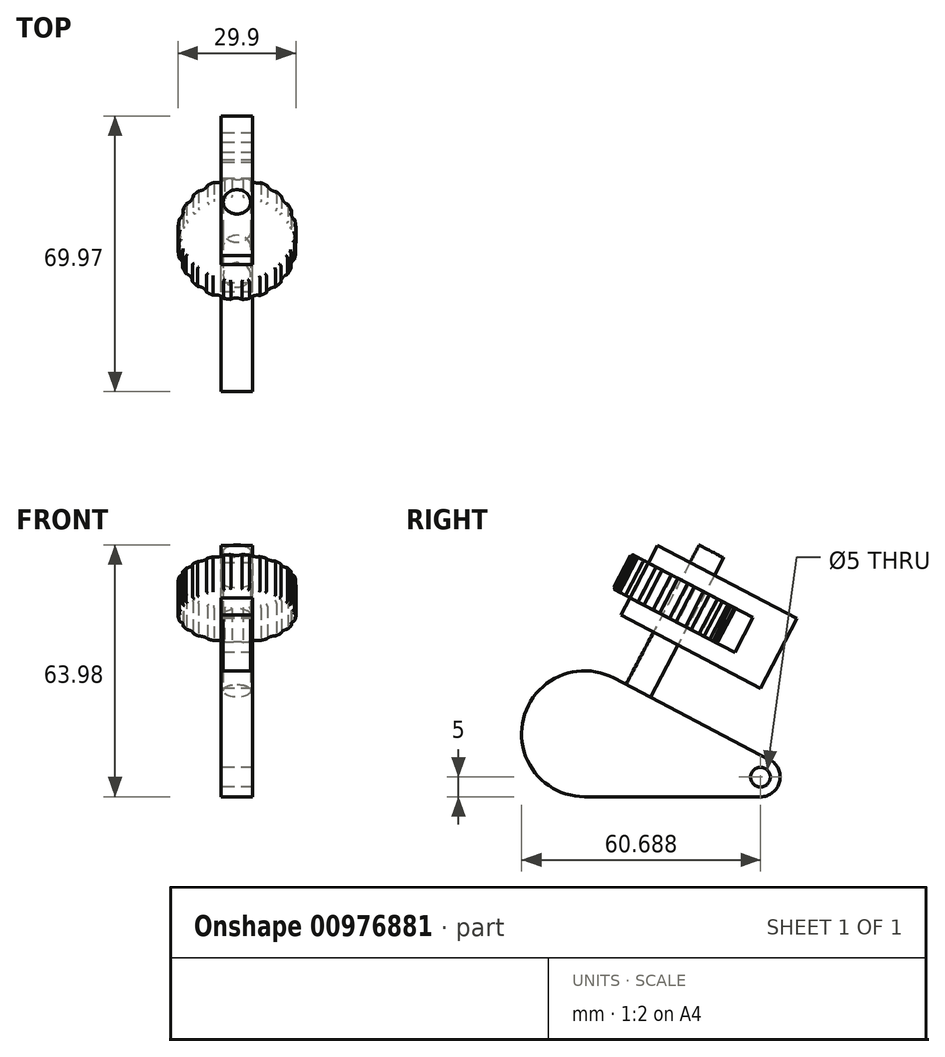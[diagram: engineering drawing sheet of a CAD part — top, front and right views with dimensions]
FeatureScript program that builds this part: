
annotation { "Feature Type Name" : "Feature", "Feature Type Description" : "" }
export const myFeature = defineFeature(function(context is Context, id is Id, definition is map)
    precondition{}
    {
        {
            var Q0;
            Q0=qCreatedBy(makeId("Right.planeOp"),FACE);
            var sketch = newSketch(context, id + "F0", { "sketchPlane" : qUnion([Q0])});
            skCircle(sketch, "E0", {"center": v(0, 0) * mm, "radius": 16 * mm});
            skLineSegment(sketch, "E1", {"start": v(35.46, -16) * mm, "end": v(40.22, -16) * mm});
            skLineSegment(sketch, "E2", {"start": v(47, -6.57) * mm, "end": v(7.43, 14.17) * mm});
            skPoint(sketch, "E3.visualSharp", {"position": v(65, -16) * mm});
            skArc(sketch, "E3.filletArc", {"start": v(44.69, -16) * mm, "mid": v(49.54, -12.2) * mm, "end": v(47, -6.57) * mm});
            skCircle(sketch, "E4", {"center": v(44.69, -11) * mm, "radius": 2.5 * mm});
            skCircle(sketch, "E5", {"center": v(0, 0) * mm, "radius": 35 * mm, "construction": true});
            skArc(sketch, "E6", {"start": v(34.54, -14.61) * mm, "mid": v(35.92, -10.78) * mm, "end": v(36.87, -6.82) * mm});
            skArc(sketch, "E7", {"start": v(40.96, -7.67) * mm, "mid": v(39.69, -11) * mm, "end": v(40.96, -14.33) * mm});
            skLineSegment(sketch, "E8", {"start": v(40.22, -6) * mm, "end": v(37.86, -6) * mm});
            skPoint(sketch, "E9.visualSharp", {"position": v(44.69, -6) * mm});
            skArc(sketch, "E9.filletArc", {"start": v(40.96, -7.67) * mm, "mid": v(41.13, -6.6) * mm, "end": v(40.22, -6) * mm});
            skPoint(sketch, "E10.visualSharp", {"position": v(37.02, -6) * mm});
            skArc(sketch, "E10.filletArc", {"start": v(37.86, -6) * mm, "mid": v(37.22, -6.23) * mm, "end": v(36.87, -6.82) * mm});
            skPoint(sketch, "E11.visualSharp", {"position": v(44.69, -16) * mm});
            skArc(sketch, "E11.filletArc", {"start": v(40.22, -16) * mm, "mid": v(41.13, -15.4) * mm, "end": v(40.96, -14.33) * mm});
            skPoint(sketch, "E12.newPointB", {"position": v(0, -16) * mm});
            skArc(sketch, "E12.filletArc", {"start": v(34.54, -14.61) * mm, "mid": v(34.62, -15.55) * mm, "end": v(35.46, -16) * mm});
            skLineSegment(sketch, "E13", {"start": v(35.46, -16) * mm, "end": v(0, -16) * mm});
            skLineSegment(sketch, "E14", {"start": v(40.22, -16) * mm, "end": v(44.69, -16) * mm});
            skSolve(sketch);
        }
        {
            var Q0;
            {var subQ0=sQuery(id+"F0.wireOp",EDGE,"E0");var subQ1=makeQuery(id+"F0.imprint","INTERSECT",VERTEX,{"derivedFrom":[subQ0,sQuery(id+"F0.wireOp",EDGE,"E2")]});Q0=makeQuery(id+"F0.imprint","IMPRINT",FACE,{"disambiguationData":[TD([[makeQuery(id+"F0.imprint","IMPRINT",EDGE,{"disambiguationData":[TD([[subQ1,-1.0]])],"derivedFrom":subQ0}),1.0]])]});}
            var Q1;
            {var subQ0=sQuery(id+"F0.wireOp",EDGE,"E2");Q1=makeQuery(id+"F0.imprint","IMPRINT",FACE,{"disambiguationData":[TD([[makeQuery(id+"F0.imprint","IMPRINT",EDGE,{"derivedFrom":subQ0}),1.0]])]});}
            var Q2;
            Q2=makeQuery(id+"F0.imprint","IMPRINT",FACE,{"disambiguationData":[TD([[makeQuery(id+"F0.imprint","IMPRINT",EDGE,{"derivedFrom":sQuery(id+"F0.wireOp",EDGE,"E1")}),1.0]])]});
            extrude(context, id + "F1", {"entities" : qUnion([Q0, Q1, Q2]), "depth" : 8 * mm, "offsetDistance" : 25 * mm});
        }
        {
            var Q0;
            Q0=makeQuery(id+"F1.opExtrude","SWEPT_FACE",FACE,{"disambiguationData":[OSD([sQuery(id+"F0.wireOp",EDGE,"E2")])]});
            var sketch = newSketch(context, id + "F2", { "sketchPlane" : qUnion([Q0])});
            skCircle(sketch, "E15", {"center": v(4, 7) * mm, "radius": 3.5 * mm});
            skPoint(sketch, "E15.centerSnap0", {"position": v(4, 0) * mm});
            skSolve(sketch);
        }
        {
            var Q0;
            {var subQ0=sQuery(id+"F2.wireOp",EDGE,"E15");var subQ1=sQuery(id+"F0.wireOp",EDGE,"E2");var subQ2=makeQuery(id+"F2.imprint","INTERSECT",VERTEX,{"derivedFrom":[makeQuery(id+"F1.opExtrude","CAP_EDGE",EDGE,{"disambiguationData":[OSD([subQ1])],"isStart":true}),subQ0]});Q0=makeQuery(id+"F2.imprint","IMPRINT",FACE,{"disambiguationData":[TD([[makeQuery(id+"F2.imprint","IMPRINT",EDGE,{"disambiguationData":[TD([[subQ2,1.0]])],"derivedFrom":subQ0}),1.0]])]});}
            extrude(context, id + "F3", {"entities" : qUnion([Q0]), "depth" : 40 * mm, "offsetDistance" : 25 * mm});
        }
        {
            var Q0;
            Q0=qCreatedBy(makeId("Right.planeOp"),FACE);
            var sketch = newSketch(context, id + "F4", { "sketchPlane" : qUnion([Q0])});
            skLineSegment(sketch, "E16", {"start": v(9.26, 30.15) * mm, "end": v(44.69, 11.58) * mm});
            skLineSegment(sketch, "E17", {"start": v(9.26, 30.15) * mm, "end": v(11.58, 34.58) * mm});
            skLineSegment(sketch, "E18", {"start": v(11.58, 34.58) * mm, "end": v(38.15, 20.65) * mm});
            skLineSegment(sketch, "E19", {"start": v(38.15, 20.65) * mm, "end": v(42.8, 29.5) * mm});
            skLineSegment(sketch, "E20", {"start": v(42.8, 29.5) * mm, "end": v(16.22, 43.43) * mm});
            skLineSegment(sketch, "E21", {"start": v(16.22, 43.43) * mm, "end": v(18.54, 47.86) * mm});
            skLineSegment(sketch, "E22", {"start": v(18.54, 47.86) * mm, "end": v(53.97, 29.3) * mm});
            skLineSegment(sketch, "E23", {"start": v(53.97, 29.3) * mm, "end": v(44.69, 11.58) * mm});
            skSolve(sketch);
        }
        {
            var Q0;
            Q0=makeQuery(id+"F4.imprint","IMPRINT",FACE,{"disambiguationData":[TD([[makeQuery(id+"F4.imprint","IMPRINT",EDGE,{"derivedFrom":sQuery(id+"F4.wireOp",EDGE,"E16")}),1.0]])]});
            extrude(context, id + "F5", {"entities" : qUnion([Q0]), "depth" : 8 * mm, "offsetDistance" : 25 * mm});
        }
        {
            var Q0;
            Q0=makeQuery(id+"F5.opExtrude","SWEPT_FACE",FACE,{"disambiguationData":[OSD([sQuery(id+"F4.wireOp",EDGE,"E18")])]});
            var sketch = newSketch(context, id + "F6", { "sketchPlane" : qUnion([Q0])});
            skCircle(sketch, "E24", {"center": v(4, 4.2) * mm, "radius": 15 * mm});
            skPoint(sketch, "E24.centerSnap0", {"position": v(4, -5.8) * mm});
            skLineSegment(sketch, "E25", {"start": v(3.83, -10.8) * mm, "end": v(3.83, -12.8) * mm});
            skCircle(sketch, "E26", {"center": v(3.83, -12.8) * mm, "radius": 2.5 * mm});
            skCircle(sketch, "E27.1.0", {"center": v(9.1, -12.01) * mm, "radius": 2.5 * mm});
            skCircle(sketch, "E27.2.0", {"center": v(13.86, -9.64) * mm, "radius": 2.5 * mm});
            skCircle(sketch, "E27.3.0", {"center": v(17.66, -5.92) * mm, "radius": 2.5 * mm});
            skCircle(sketch, "E27.4.0", {"center": v(20.12, -1.2) * mm, "radius": 2.5 * mm});
            skCircle(sketch, "E27.5.0", {"center": v(21, 4.04) * mm, "radius": 2.5 * mm});
            skCircle(sketch, "E27.6.0", {"center": v(20.22, 9.3) * mm, "radius": 2.5 * mm});
            skCircle(sketch, "E27.7.0", {"center": v(17.85, 14.06) * mm, "radius": 2.5 * mm});
            skCircle(sketch, "E27.8.0", {"center": v(14.13, 17.86) * mm, "radius": 2.5 * mm});
            skCircle(sketch, "E27.9.0", {"center": v(9.41, 20.32) * mm, "radius": 2.5 * mm});
            skCircle(sketch, "E27.10.0", {"center": v(4.17, 21.2) * mm, "radius": 2.5 * mm});
            skCircle(sketch, "E27.11.0", {"center": v(-1.1, 20.42) * mm, "radius": 2.5 * mm});
            skCircle(sketch, "E27.12.0", {"center": v(-5.86, 18.06) * mm, "radius": 2.5 * mm});
            skCircle(sketch, "E27.13.0", {"center": v(-9.66, 14.33) * mm, "radius": 2.5 * mm});
            skCircle(sketch, "E27.14.0", {"center": v(-12.12, 9.62) * mm, "radius": 2.5 * mm});
            skCircle(sketch, "E27.15.0", {"center": v(-13, 4.37) * mm, "radius": 2.5 * mm});
            skCircle(sketch, "E27.16.0", {"center": v(-12.22, -0.89) * mm, "radius": 2.5 * mm});
            skCircle(sketch, "E27.17.0", {"center": v(-9.85, -5.65) * mm, "radius": 2.5 * mm});
            skCircle(sketch, "E27.18.0", {"center": v(-6.13, -9.45) * mm, "radius": 2.5 * mm});
            skCircle(sketch, "E27.19.0", {"center": v(-1.41, -11.9) * mm, "radius": 2.5 * mm});
            skCircle(sketch, "E28", {"center": v(4, 4.2) * mm, "radius": 3.5 * mm});
            skSolve(sketch);
        }
        {
            var Q0;
            {var subQ56=sQuery(id+"F4.wireOp",EDGE,"E18");var subQ57=makeQuery(id+"F5.opExtrude","SWEPT_EDGE",EDGE,{"disambiguationData":[OSD([sQuery(id+"F4.wireOp",EDGE,"E17"),subQ56])]});Q0=makeQuery(id+"F6.imprint","IMPRINT",FACE,{"disambiguationData":[TD([[makeQuery(id+"F6.imprint","IMPRINT",EDGE,{"derivedFrom":subQ57}),1.0]])]});}
            var Q1;
            Q1=makeQuery(id+"F6.imprint","IMPRINT",FACE,{"disambiguationData":[TD([[makeQuery(id+"F6.imprint","IMPRINT",EDGE,{"derivedFrom":sQuery(id+"F6.wireOp",EDGE,"E28")}),-1.0]])]});
            extrude(context, id + "F7", {"entities" : qUnion([Q0, Q1]), "depth" : 10 * mm, "offsetDistance" : 25 * mm});
        }
        {
            var Q0;
            Q0=makeQuery(id+"F7.opExtrude","CAP_FACE",FACE,{"disambiguationData":[OSD([sQuery(id+"F6.wireOp",EDGE,"E24"),sQuery(id+"F6.wireOp",EDGE,"E26"),sQuery(id+"F6.wireOp",EDGE,"E27.1.0"),sQuery(id+"F6.wireOp",EDGE,"E27.2.0"),sQuery(id+"F6.wireOp",EDGE,"E27.3.0"),sQuery(id+"F6.wireOp",EDGE,"E27.4.0"),sQuery(id+"F6.wireOp",EDGE,"E27.5.0"),sQuery(id+"F6.wireOp",EDGE,"E27.6.0"),sQuery(id+"F6.wireOp",EDGE,"E27.7.0"),sQuery(id+"F6.wireOp",EDGE,"E27.8.0"),sQuery(id+"F6.wireOp",EDGE,"E27.9.0"),sQuery(id+"F6.wireOp",EDGE,"E27.10.0"),sQuery(id+"F6.wireOp",EDGE,"E27.11.0"),sQuery(id+"F6.wireOp",EDGE,"E27.12.0"),sQuery(id+"F6.wireOp",EDGE,"E27.13.0"),sQuery(id+"F6.wireOp",EDGE,"E27.14.0"),sQuery(id+"F6.wireOp",EDGE,"E27.15.0"),sQuery(id+"F6.wireOp",EDGE,"E27.16.0"),sQuery(id+"F6.wireOp",EDGE,"E27.17.0"),sQuery(id+"F6.wireOp",EDGE,"E27.18.0"),sQuery(id+"F6.wireOp",EDGE,"E27.19.0"),sQuery(id+"F6.wireOp",EDGE,"E28")])],"isStart":false});
            var Q1;
            Q1=makeQuery(id+"F7.opExtrude","CAP_FACE",FACE,{"disambiguationData":[OSD([sQuery(id+"F6.wireOp",EDGE,"E24"),sQuery(id+"F6.wireOp",EDGE,"E26"),sQuery(id+"F6.wireOp",EDGE,"E27.1.0"),sQuery(id+"F6.wireOp",EDGE,"E27.2.0"),sQuery(id+"F6.wireOp",EDGE,"E27.3.0"),sQuery(id+"F6.wireOp",EDGE,"E27.4.0"),sQuery(id+"F6.wireOp",EDGE,"E27.5.0"),sQuery(id+"F6.wireOp",EDGE,"E27.6.0"),sQuery(id+"F6.wireOp",EDGE,"E27.7.0"),sQuery(id+"F6.wireOp",EDGE,"E27.8.0"),sQuery(id+"F6.wireOp",EDGE,"E27.9.0"),sQuery(id+"F6.wireOp",EDGE,"E27.10.0"),sQuery(id+"F6.wireOp",EDGE,"E27.11.0"),sQuery(id+"F6.wireOp",EDGE,"E27.12.0"),sQuery(id+"F6.wireOp",EDGE,"E27.13.0"),sQuery(id+"F6.wireOp",EDGE,"E27.14.0"),sQuery(id+"F6.wireOp",EDGE,"E27.15.0"),sQuery(id+"F6.wireOp",EDGE,"E27.16.0"),sQuery(id+"F6.wireOp",EDGE,"E27.17.0"),sQuery(id+"F6.wireOp",EDGE,"E27.18.0"),sQuery(id+"F6.wireOp",EDGE,"E27.19.0"),sQuery(id+"F6.wireOp",EDGE,"E28")])],"isStart":true});
            fillet(context, id + "F8", {"entities" : qUnion([Q0, Q1]), "radius" : 0.5 * mm, "tangentPropagation" : true, "allowEdgeOverflow" : false});
        }
    });
